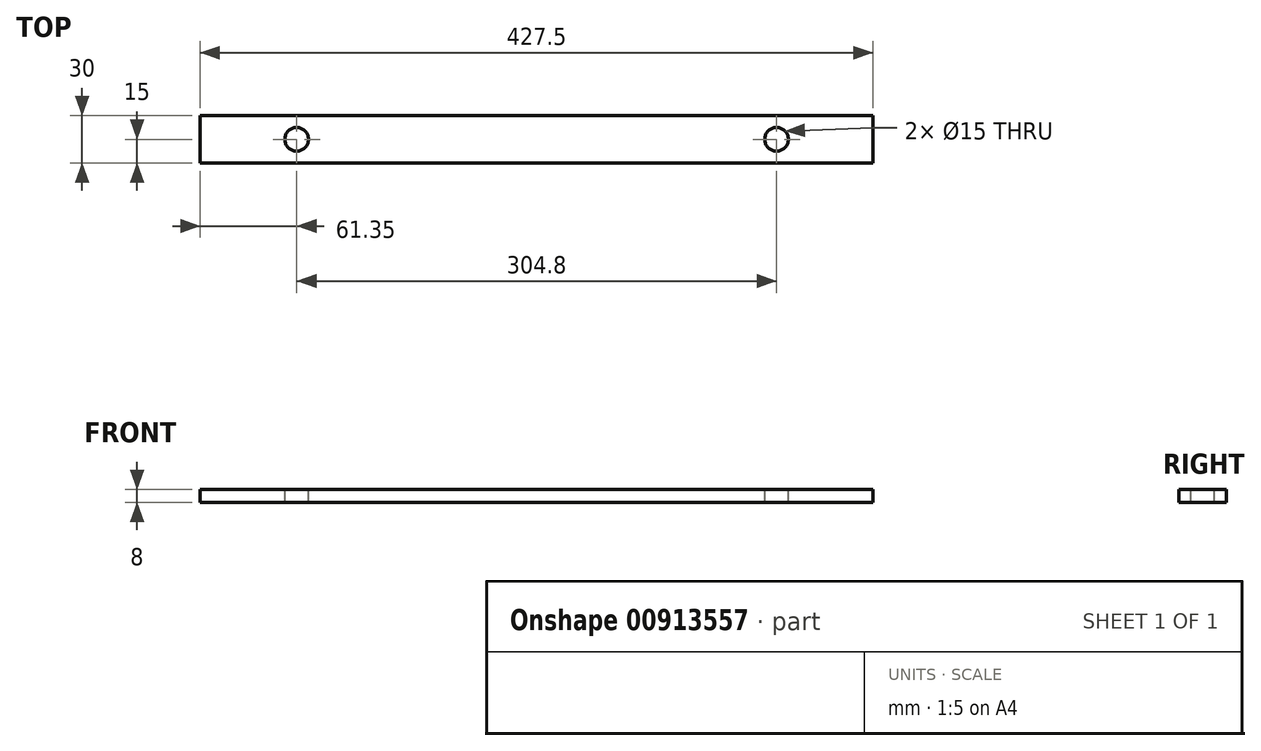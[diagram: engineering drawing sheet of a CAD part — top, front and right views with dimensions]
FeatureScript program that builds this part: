
annotation { "Feature Type Name" : "Feature", "Feature Type Description" : "" }
export const myFeature = defineFeature(function(context is Context, id is Id, definition is map)
    precondition{}
    {
        {
            var Q0;
            Q0=qCreatedBy(makeId("Top.planeOp"),FACE);
            var sketch = newSketch(context, id + "F0", { "sketchPlane" : qUnion([Q0])});
            skLineSegment(sketch, "E0.bottom", {"start": v(-213.75, 15) * mm, "end": v(213.75, 15) * mm});
            skLineSegment(sketch, "E0.top", {"start": v(-213.75, -15) * mm, "end": v(213.75, -15) * mm});
            skLineSegment(sketch, "E0.left", {"start": v(-213.75, 15) * mm, "end": v(-213.75, -15) * mm});
            skLineSegment(sketch, "E0.right", {"start": v(213.75, 15) * mm, "end": v(213.75, -15) * mm});
            skPoint(sketch, "E0.middle", {"position": v(0, 0) * mm});
            skSolve(sketch);
        }
        {
            var Q0;
            Q0=makeQuery(id+"F0.imprint","IMPRINT",FACE,{"disambiguationData":[TD([[makeQuery(id+"F0.imprint","IMPRINT",EDGE,{"derivedFrom":sQuery(id+"F0.wireOp",EDGE,"E0.bottom")}),-1.0]])]});
            extrude(context, id + "F1", {"entities" : qUnion([Q0]), "depth" : 8 * mm, "offsetDistance" : 25 * mm});
        }
        {
            var Q0;
            Q0=makeQuery(id+"F1.opExtrude","CAP_FACE",FACE,{"disambiguationData":[OSD([sQuery(id+"F0.wireOp",EDGE,"E0.bottom"),sQuery(id+"F0.wireOp",EDGE,"E0.top"),sQuery(id+"F0.wireOp",EDGE,"E0.left"),sQuery(id+"F0.wireOp",EDGE,"E0.right")])],"isStart":false});
            var sketch = newSketch(context, id + "F2", { "sketchPlane" : qUnion([Q0])});
            skPoint(sketch, "E1", {"position": v(-152.4, 0) * mm});
            skPoint(sketch, "E2", {"position": v(152.4, 0) * mm});
            skSolve(sketch);
        }
        {
            var Q0;
            Q0=sQuery(id+"F2.wireOp",VERTEX,"E2");
            var Q1;
            Q1=sQuery(id+"F2.wireOp",VERTEX,"E1");
            var Q2;
            Q2=makeQuery(id+"F1.opExtrude","SWEPT_BODY",BODY,{"disambiguationData":[OSD([sQuery(id+"F0.wireOp",EDGE,"E0.bottom"),sQuery(id+"F0.wireOp",EDGE,"E0.top"),sQuery(id+"F0.wireOp",EDGE,"E0.left"),sQuery(id+"F0.wireOp",EDGE,"E0.right")])]});
            hole(context, id + "F3", {"style" : HoleStyle.SIMPLE, "endStyle" : HoleEndStyle.THROUGH, "holeDiameter" : 15 * mm, "majorDiameter" : 5 * mm, "isTappedThrough" : true, "tappedDepth" : 12 * mm, "tapClearance" : 3, "locations" : qUnion([Q0, Q1]), "scope" : qUnion([Q2])});
        }
    });
